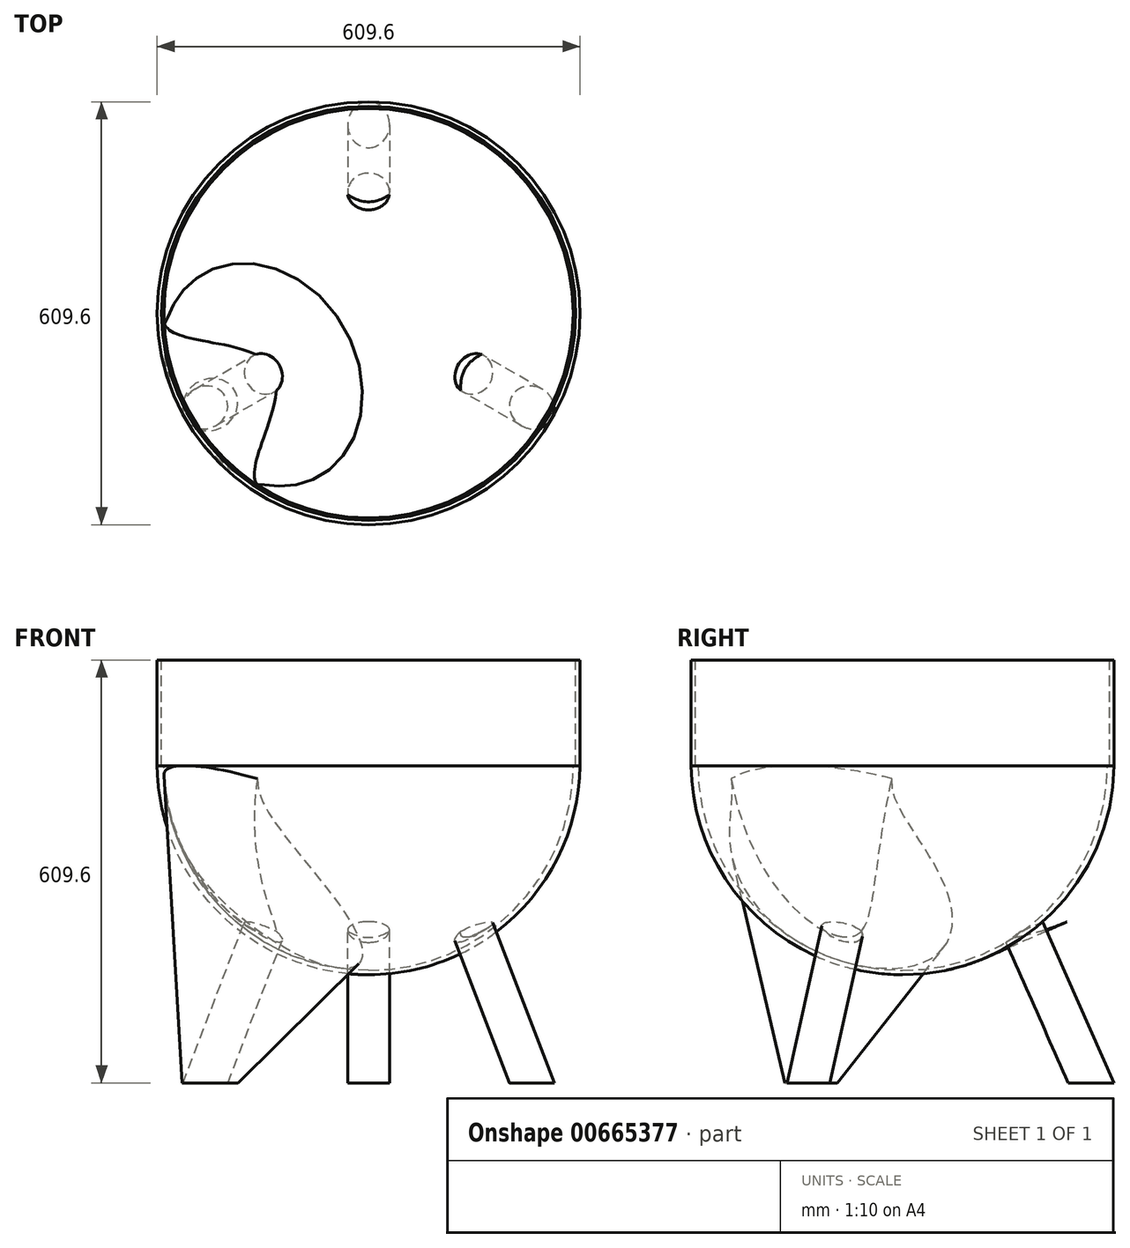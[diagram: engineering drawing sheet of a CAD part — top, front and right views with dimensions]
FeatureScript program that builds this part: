
annotation { "Feature Type Name" : "Feature", "Feature Type Description" : "" }
export const myFeature = defineFeature(function(context is Context, id is Id, definition is map)
    precondition{}
    {
        {
            var Q0;
            Q0=qCreatedBy(makeId("Top.planeOp"),FACE);
            var sketch = newSketch(context, id + "F0", { "sketchPlane" : qUnion([Q0])});
            skCircle(sketch, "E0.cCircle", {"center": v(0, 0) * mm, "radius": 527.93 * mm, "construction": true});
            skLineSegment(sketch, "E0.0", {"start": v(304.8, 527.93) * mm, "end": v(609.6, 0) * mm});
            skLineSegment(sketch, "E0.1", {"start": v(609.6, 0) * mm, "end": v(457.2, -263.96) * mm});
            skLineSegment(sketch, "E0.2", {"start": v(304.8, -527.93) * mm, "end": v(-304.8, -527.93) * mm});
            skLineSegment(sketch, "E0.3", {"start": v(-304.8, -527.93) * mm, "end": v(-457.2, -263.96) * mm});
            skLineSegment(sketch, "E0.4", {"start": v(-609.6, 0) * mm, "end": v(-447.68, 280.46) * mm});
            skLineSegment(sketch, "E0.5", {"start": v(-304.8, 527.93) * mm, "end": v(0, 527.93) * mm});
            skPoint(sketch, "E0.0.midPoint", {"position": v(457.2, 263.96) * mm});
            skCircle(sketch, "E1", {"center": v(0, 0) * mm, "radius": 304.8 * mm});
            skLineSegment(sketch, "E2", {"start": v(-466.73, 247.47) * mm, "end": v(-272.97, 135.6) * mm});
            skLineSegment(sketch, "E3", {"start": v(-447.68, 280.46) * mm, "end": v(-253.92, 168.6) * mm});
            skLineSegment(sketch, "E4", {"start": v(-304.8, 527.93) * mm, "end": v(-304.8, 527.93) * mm});
            skLineSegment(sketch, "E5", {"start": v(-466.73, 247.47) * mm, "end": v(-304.8, 527.93) * mm});
            skLineSegment(sketch, "E6", {"start": v(-447.68, 280.46) * mm, "end": v(-401.2, 360.95) * mm});
            skLineSegment(sketch, "E7", {"start": v(-609.6, 0) * mm, "end": v(-609.6, 0) * mm});
            skLineSegment(sketch, "E8.1.0", {"start": v(-447.68, -280.46) * mm, "end": v(-253.92, -168.6) * mm});
            skLineSegment(sketch, "E8.1.1", {"start": v(-466.73, -247.47) * mm, "end": v(-272.97, -135.6) * mm});
            skLineSegment(sketch, "E8.2.0", {"start": v(19.05, -527.93) * mm, "end": v(19.05, -304.2) * mm});
            skLineSegment(sketch, "E8.2.1", {"start": v(-19.05, -527.93) * mm, "end": v(-19.05, -304.2) * mm});
            skLineSegment(sketch, "E8.3.0", {"start": v(466.73, -247.47) * mm, "end": v(272.97, -135.6) * mm});
            skLineSegment(sketch, "E8.3.1", {"start": v(447.68, -280.46) * mm, "end": v(253.92, -168.6) * mm});
            skLineSegment(sketch, "E8.4.0", {"start": v(447.68, 280.46) * mm, "end": v(253.92, 168.6) * mm});
            skLineSegment(sketch, "E8.4.1", {"start": v(466.73, 247.47) * mm, "end": v(272.97, 135.6) * mm});
            skLineSegment(sketch, "E8.5.0", {"start": v(-19.05, 527.93) * mm, "end": v(-19.05, 304.2) * mm});
            skLineSegment(sketch, "E8.5.1", {"start": v(19.05, 527.93) * mm, "end": v(19.05, 304.2) * mm});
            skLineSegment(sketch, "E9", {"start": v(-1099.5, 304.8) * mm, "end": v(1284.02, 304.8) * mm, "construction": true});
            skLineSegment(sketch, "E10", {"start": v(-1101.82, -304.8) * mm, "end": v(1466.6, -304.8) * mm, "construction": true});
            skLineSegment(sketch, "E11", {"start": v(127, -73.32) * mm, "end": v(-127, -73.32) * mm});
            skCircle(sketch, "E12", {"center": v(0, 0) * mm, "radius": 146.65 * mm, "construction": true});
            skLineSegment(sketch, "E13", {"start": v(0, 0) * mm, "end": v(263.96, -152.4) * mm, "construction": true});
            skLineSegment(sketch, "E14", {"start": v(0, 0) * mm, "end": v(-263.96, -152.4) * mm, "construction": true});
            skLineSegment(sketch, "E15", {"start": v(0, 0) * mm, "end": v(0, 304.8) * mm, "construction": true});
            skLineSegment(sketch, "E16", {"start": v(263.96, -152.4) * mm, "end": v(1171.58, -676.41) * mm, "construction": true});
            skLineSegment(sketch, "E17", {"start": v(457.2, -263.96) * mm, "end": v(304.8, -527.93) * mm});
            skLineSegment(sketch, "E18", {"start": v(263.96, -152.4) * mm, "end": v(457.2, -263.96) * mm});
            skLineSegment(sketch, "E19", {"start": v(0, 304.8) * mm, "end": v(0, 1090.4) * mm, "construction": true});
            skLineSegment(sketch, "E20", {"start": v(0, 527.93) * mm, "end": v(304.8, 527.93) * mm});
            skLineSegment(sketch, "E21", {"start": v(0, 527.93) * mm, "end": v(0, 304.8) * mm});
            skLineSegment(sketch, "E22", {"start": v(-263.96, -152.4) * mm, "end": v(-1262.9, -729.14) * mm, "construction": true});
            skLineSegment(sketch, "E23", {"start": v(-457.2, -263.96) * mm, "end": v(-609.6, 0) * mm});
            skLineSegment(sketch, "E24", {"start": v(-263.96, -152.4) * mm, "end": v(-457.2, -263.96) * mm});
            skCircle(sketch, "E25", {"center": v(0, 0) * mm, "radius": 298.45 * mm});
            skSolve(sketch);
        }
        {
            var Q0;
            {var subQ0=sQuery(id+"F0.wireOp",EDGE,"E1");var subQ8=makeQuery(id+"F0.imprint","INTERSECT",VERTEX,{"derivedFrom":[subQ0,sQuery(id+"F0.wireOp",EDGE,"E8.4.0")]});Q0=makeQuery(id+"F0.imprint","IMPRINT",FACE,{"disambiguationData":[TD([[makeQuery(id+"F0.imprint","IMPRINT",EDGE,{"disambiguationData":[TD([[subQ8,1.0]])],"derivedFrom":subQ0}),1.0]])]});}
            extrude(context, id + "F1", {"entities" : qUnion([Q0]), "oppositeDirection" : true, "depth" : 152.4 * mm, "offsetDistance" : 25.4 * mm, "hasSecondDirection" : true, "secondDirectionOppositeDirection" : true, "secondDirectionDepth" : 0 * mm});
        }
        {
            var Q0;
            Q0=qCreatedBy(makeId("Front.planeOp"),FACE);
            var sketch = newSketch(context, id + "F2", { "sketchPlane" : qUnion([Q0])});
            skLineSegment(sketch, "E26", {"start": v(0, 608.83) * mm, "end": v(0, -1105.26) * mm, "construction": true});
            skLineSegment(sketch, "E27", {"start": v(-304.8, 462.6) * mm, "end": v(-304.8, -843.09) * mm});
            skLineSegment(sketch, "E28.MirrorCS", {"start": v(304.8, 462.6) * mm, "end": v(304.8, -843.09) * mm});
            skLineSegment(sketch, "E29", {"start": v(-1108.33, -152.4) * mm, "end": v(1492.5, -152.4) * mm, "construction": true});
            skArc(sketch, "E30", {"start": v(-304.8, -152.4) * mm, "mid": v(-214.3, -365.69) * mm, "end": v(0, -453.74) * mm});
            skArc(sketch, "E31", {"start": v(0, -453.74) * mm, "mid": v(214.3, -365.69) * mm, "end": v(304.8, -152.4) * mm});
            skLineSegment(sketch, "E32", {"start": v(-495.68, -152.4) * mm, "end": v(0, -152.4) * mm});
            skLineSegment(sketch, "E33", {"start": v(0, 45.3) * mm, "end": v(0, -541.67) * mm});
            skLineSegment(sketch, "E34", {"start": v(0, -152.4) * mm, "end": v(518.85, -152.4) * mm});
            skCircle(sketch, "E35", {"center": v(0, -152.4) * mm, "radius": 294.99 * mm});
            skSolve(sketch);
        }
        {
            var Q0;
            Q0=sQuery(id+"F0.wireOp",EDGE,"E13");
            var Q1;
            Q1=sQuery(id+"F2.wireOp",EDGE,"E26");
            cPlane(context, id + "F3", {"entities" : qUnion([Q0, Q1]), "cplaneType" : CPlaneType.LINE_ANGLE, "offset" : 25.4 * mm, "angle" : 0 * degree, "width" : 152.4 * mm, "height" : 152.4 * mm});
        }
        {
            var Q0;
            Q0=sQuery(id+"F0.wireOp",EDGE,"E15");
            var Q1;
            Q1=sQuery(id+"F2.wireOp",EDGE,"E26");
            cPlane(context, id + "F4", {"entities" : qUnion([Q0, Q1]), "cplaneType" : CPlaneType.LINE_ANGLE, "offset" : 25.4 * mm, "angle" : 0 * degree, "width" : 152.4 * mm, "height" : 152.4 * mm});
        }
        {
            var Q0;
            Q0=sQuery(id+"F0.wireOp",EDGE,"E22");
            var Q1;
            Q1=sQuery(id+"F2.wireOp",EDGE,"E26");
            cPlane(context, id + "F5", {"entities" : qUnion([Q0, Q1]), "cplaneType" : CPlaneType.LINE_ANGLE, "offset" : 25.4 * mm, "angle" : 0 * degree, "width" : 152.4 * mm, "height" : 152.4 * mm});
        }
        {
            var Q0;
            Q0=qCreatedBy(id+"F5.planeOp",FACE);
            var sketch = newSketch(context, id + "F6", { "sketchPlane" : qUnion([Q0])});
            skLineSegment(sketch, "E36", {"start": v(-1017.96, -609.6) * mm, "end": v(1871, -609.6) * mm});
            skLineSegment(sketch, "E37", {"start": v(0, 853.8) * mm, "end": v(0, -860.28) * mm, "construction": true});
            skLineSegment(sketch, "E38", {"start": v(-304.8, 707.57) * mm, "end": v(-304.8, -609.6) * mm});
            skArc(sketch, "E39", {"start": v(-304.8, -152.4) * mm, "mid": v(-214.3, -365.69) * mm, "end": v(0, -453.74) * mm});
            skArc(sketch, "E40", {"start": v(0, -453.74) * mm, "mid": v(214.3, -365.69) * mm, "end": v(304.8, -152.4) * mm});
            skLineSegment(sketch, "E41", {"start": v(0, -152.4) * mm, "end": v(451.52, -152.4) * mm, "construction": true});
            skLineSegment(sketch, "E42", {"start": v(-1487.46, 0) * mm, "end": v(0, 0) * mm, "construction": true});
            skLineSegment(sketch, "E43", {"start": v(-470.85, 0) * mm, "end": v(0, 0) * mm, "construction": true});
            skLineSegment(sketch, "E44", {"start": v(317.12, -609.6) * mm, "end": v(386.78, -609.6) * mm});
            skLineSegment(sketch, "E45", {"start": v(-1.48, 0.66) * mm, "end": v(-271.74, -609.6) * mm});
            skLineSegment(sketch, "E46", {"start": v(-34.83, 0) * mm, "end": v(-304.8, -609.6) * mm});
            skLineSegment(sketch, "E47.MirrorCS", {"start": v(20.45, -24.48) * mm, "end": v(-238.69, -609.6) * mm});
            skLineSegment(sketch, "E48.MirrorCS", {"start": v(-20.45, -24.48) * mm, "end": v(238.69, -609.6) * mm});
            skLineSegment(sketch, "E49.MirrorCS", {"start": v(1.48, 0.66) * mm, "end": v(271.74, -609.6) * mm});
            skLineSegment(sketch, "E50.MirrorCS", {"start": v(34.83, 0) * mm, "end": v(304.8, -609.6) * mm});
            skSolve(sketch);
        }
        {
            var Q0;
            Q0=qCreatedBy(id+"F3.planeOp",FACE);
            var sketch = newSketch(context, id + "F7", { "sketchPlane" : qUnion([Q0])});
            skLineSegment(sketch, "E51", {"start": v(-772.12, 911.8) * mm, "end": v(-772.12, 687.46) * mm, "construction": true});
            skLineSegment(sketch, "E52", {"start": v(-1017.96, -609.6) * mm, "end": v(1871, -609.6) * mm});
            skLineSegment(sketch, "E53", {"start": v(-2207.22, 0) * mm, "end": v(364.68, 0) * mm, "construction": true});
            skLineSegment(sketch, "E54", {"start": v(0, 1066.37) * mm, "end": v(0, -647.72) * mm, "construction": true});
            skLineSegment(sketch, "E55", {"start": v(-304.8, 707.57) * mm, "end": v(-304.8, -609.6) * mm});
            skLineSegment(sketch, "E56", {"start": v(-2149.32, -152.4) * mm, "end": v(0, -152.4) * mm, "construction": true});
            skArc(sketch, "E57", {"start": v(-304.8, -152.4) * mm, "mid": v(-214.3, -365.69) * mm, "end": v(0, -453.74) * mm});
            skArc(sketch, "E58", {"start": v(0, -453.74) * mm, "mid": v(214.3, -365.69) * mm, "end": v(304.8, -152.4) * mm});
            skLineSegment(sketch, "E59", {"start": v(0, -152.4) * mm, "end": v(451.52, -152.4) * mm, "construction": true});
            skLineSegment(sketch, "E60", {"start": v(-1475.42, 0) * mm, "end": v(0, 0) * mm, "construction": true});
            skLineSegment(sketch, "E61", {"start": v(-458.8, 0) * mm, "end": v(0, 0) * mm, "construction": true});
            skLineSegment(sketch, "E62", {"start": v(317.12, -609.6) * mm, "end": v(386.78, -609.6) * mm});
            skLineSegment(sketch, "E63", {"start": v(-1.48, 0.66) * mm, "end": v(-271.74, -609.6) * mm});
            skLineSegment(sketch, "E64", {"start": v(-34.83, 0) * mm, "end": v(-304.8, -609.6) * mm});
            skLineSegment(sketch, "E65.MirrorCS", {"start": v(20.45, -24.48) * mm, "end": v(-238.69, -609.6) * mm});
            skLineSegment(sketch, "E66.MirrorCS", {"start": v(-20.45, -24.48) * mm, "end": v(238.69, -609.6) * mm});
            skLineSegment(sketch, "E67.MirrorCS", {"start": v(1.48, 0.66) * mm, "end": v(271.74, -609.6) * mm});
            skLineSegment(sketch, "E68.MirrorCS", {"start": v(34.83, 0) * mm, "end": v(304.8, -609.6) * mm});
            skSolve(sketch);
        }
        {
            var Q0;
            Q0=qCreatedBy(id+"F4.planeOp",FACE);
            var sketch = newSketch(context, id + "F8", { "sketchPlane" : qUnion([Q0])});
            skLineSegment(sketch, "E69", {"start": v(-772.12, 911.8) * mm, "end": v(-772.12, 687.46) * mm, "construction": true});
            skLineSegment(sketch, "E70", {"start": v(-1017.96, -609.6) * mm, "end": v(1871, -609.6) * mm});
            skLineSegment(sketch, "E71", {"start": v(-2207.22, 0) * mm, "end": v(364.68, 0) * mm, "construction": true});
            skLineSegment(sketch, "E72", {"start": v(0, 1066.37) * mm, "end": v(0, -647.72) * mm, "construction": true});
            skLineSegment(sketch, "E73", {"start": v(-304.8, 707.57) * mm, "end": v(-304.8, -609.6) * mm});
            skLineSegment(sketch, "E74", {"start": v(-2149.32, -152.4) * mm, "end": v(0, -152.4) * mm, "construction": true});
            skArc(sketch, "E75", {"start": v(-304.8, -152.4) * mm, "mid": v(-214.3, -365.69) * mm, "end": v(0, -453.74) * mm});
            skArc(sketch, "E76", {"start": v(0, -453.74) * mm, "mid": v(214.3, -365.69) * mm, "end": v(304.8, -152.4) * mm});
            skLineSegment(sketch, "E77", {"start": v(0, -152.4) * mm, "end": v(451.52, -152.4) * mm, "construction": true});
            skLineSegment(sketch, "E78", {"start": v(-1475.42, 0) * mm, "end": v(0, 0) * mm, "construction": true});
            skLineSegment(sketch, "E79", {"start": v(-458.8, 0) * mm, "end": v(0, 0) * mm, "construction": true});
            skLineSegment(sketch, "E80", {"start": v(317.12, -609.6) * mm, "end": v(386.78, -609.6) * mm});
            skLineSegment(sketch, "E81", {"start": v(-1.48, 0.66) * mm, "end": v(-271.74, -609.6) * mm});
            skLineSegment(sketch, "E82", {"start": v(-34.83, 0) * mm, "end": v(-304.8, -609.6) * mm});
            skLineSegment(sketch, "E83.MirrorCS", {"start": v(20.45, -24.48) * mm, "end": v(-238.69, -609.6) * mm});
            skLineSegment(sketch, "E84.MirrorCS", {"start": v(-20.45, -24.48) * mm, "end": v(238.69, -609.6) * mm});
            skLineSegment(sketch, "E85.MirrorCS", {"start": v(1.48, 0.66) * mm, "end": v(271.74, -609.6) * mm});
            skLineSegment(sketch, "E86.MirrorCS", {"start": v(34.83, 0) * mm, "end": v(304.8, -609.6) * mm});
            skSolve(sketch);
        }
        {
            var Q0;
            {var subQ0=sQuery(id+"F2.wireOp",EDGE,"E31");Q0=makeQuery(id+"F2.imprint","IMPRINT",FACE,{"disambiguationData":[TD([[makeQuery(id+"F2.imprint","IMPRINT",EDGE,{"derivedFrom":subQ0}),1.0]])]});}
            var Q1;
            Q1=sQuery(id+"F2.wireOp",EDGE,"E33");
            revolve(context, id + "F9", {"entities" : qUnion([Q0]), "axis" : qUnion([Q1]), "revolveType" : RevolveType.FULL});
        }
        {
            var Q0;
            {var subQ0=sQuery(id+"F0.wireOp",EDGE,"E8.1.0");Q0=makeQuery(id+"F0.imprint","IMPRINT",FACE,{"disambiguationData":[TD([[makeQuery(id+"F0.imprint","IMPRINT",EDGE,{"derivedFrom":subQ0}),-1.0]])]});}
            cPlane(context, id + "F10", {"entities" : qUnion([Q0]), "cplaneType" : CPlaneType.OFFSET, "offset" : 609.6 * mm, "oppositeDirection" : true, "width" : 152.4 * mm, "height" : 152.4 * mm});
        }
        {
            var Q0;
            Q0=qCreatedBy(id+"F10.planeOp",FACE);
            var sketch = newSketch(context, id + "F11", { "sketchPlane" : qUnion([Q0])});
            skLineSegment(sketch, "E87.bottom", {"start": v(-626.3, 430.62) * mm, "end": v(641.52, 430.62) * mm});
            skLineSegment(sketch, "E87.top", {"start": v(-626.3, -585.38) * mm, "end": v(641.52, -585.38) * mm});
            skLineSegment(sketch, "E87.left", {"start": v(-626.3, 430.62) * mm, "end": v(-626.3, -585.38) * mm});
            skLineSegment(sketch, "E87.right", {"start": v(641.52, 430.62) * mm, "end": v(641.52, -585.38) * mm});
            skSolve(sketch);
        }
        {
            var Q0;
            {var subQ0=sQuery(id+"F8.wireOp",EDGE,"E82");var subQ5=sQuery(id+"F8.wireOp",EDGE,"E75");var subQ6=makeQuery(id+"F8.imprint","INTERSECT",VERTEX,{"derivedFrom":[subQ5,subQ0]});Q0=makeQuery(id+"F8.imprint","IMPRINT",FACE,{"disambiguationData":[TD([[makeQuery(id+"F8.imprint","IMPRINT",EDGE,{"disambiguationData":[TD([[subQ6,-1.0]])],"derivedFrom":subQ5}),-1.0]])]});}
            var Q1;
            Q1=sQuery(id+"F8.wireOp",EDGE,"E81");
            revolve(context, id + "F12", {"entities" : qUnion([Q0]), "axis" : qUnion([Q1]), "revolveType" : RevolveType.FULL});
        }
        {
            var Q0;
            {var subQ0=sQuery(id+"F7.wireOp",EDGE,"E64");var subQ5=sQuery(id+"F7.wireOp",EDGE,"E57");var subQ6=makeQuery(id+"F7.imprint","INTERSECT",VERTEX,{"derivedFrom":[subQ5,subQ0]});Q0=makeQuery(id+"F7.imprint","IMPRINT",FACE,{"disambiguationData":[TD([[makeQuery(id+"F7.imprint","IMPRINT",EDGE,{"disambiguationData":[TD([[subQ6,-1.0]])],"derivedFrom":subQ5}),-1.0]])]});}
            var Q1;
            Q1=sQuery(id+"F7.wireOp",EDGE,"E63");
            revolve(context, id + "F13", {"entities" : qUnion([Q0]), "axis" : qUnion([Q1]), "revolveType" : RevolveType.FULL});
        }
        {
            var Q0;
            {var subQ0=sQuery(id+"F6.wireOp",EDGE,"E46");var subQ5=sQuery(id+"F6.wireOp",EDGE,"E39");var subQ6=makeQuery(id+"F6.imprint","INTERSECT",VERTEX,{"derivedFrom":[subQ5,subQ0]});Q0=makeQuery(id+"F6.imprint","IMPRINT",FACE,{"disambiguationData":[TD([[makeQuery(id+"F6.imprint","IMPRINT",EDGE,{"disambiguationData":[TD([[subQ6,-1.0]])],"derivedFrom":subQ5}),-1.0]])]});}
            var Q1;
            Q1=sQuery(id+"F6.wireOp",EDGE,"E45");
            revolve(context, id + "F14", {"entities" : qUnion([Q0]), "axis" : qUnion([Q1]), "revolveType" : RevolveType.FULL});
        }
        {
            var Q0;
            {var subQ0=sQuery(id+"F2.wireOp",EDGE,"E34");var subQ3=sQuery(id+"F2.wireOp",EDGE,"E35");var subQ5=makeQuery(id+"F2.imprint","INTERSECT",VERTEX,{"derivedFrom":[subQ0,subQ3]});Q0=makeQuery(id+"F2.imprint","IMPRINT",FACE,{"disambiguationData":[TD([[makeQuery(id+"F2.imprint","IMPRINT",EDGE,{"disambiguationData":[TD([[subQ5,1.0]])],"derivedFrom":subQ3}),1.0]])]});}
            var Q1;
            Q1=sQuery(id+"F2.wireOp",EDGE,"E33");
            revolve(context, id + "F15", {"operationType" : NewBodyOperationType.REMOVE, "entities" : qUnion([Q0]), "axis" : qUnion([Q1]), "revolveType" : RevolveType.FULL, "oppositeDirection" : true});
        }
        {
            var Q0;
            Q0 = qSketchRegion(id + "F11", true);
            extrude(context, id + "F16", {"entities" : qUnion([Q0]), "operationType" : NewBodyOperationType.REMOVE, "oppositeDirection" : true, "depth" : 76.2 * mm, "offsetDistance" : 25.4 * mm});
        }
    });
